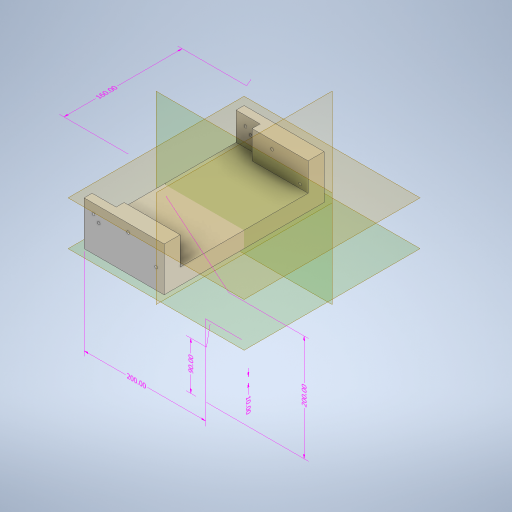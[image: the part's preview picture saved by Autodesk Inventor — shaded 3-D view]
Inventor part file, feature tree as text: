
AUTODESK INVENTOR PART (.ipt)
format: ipt  version: 2023 (Build 270158000, 158)  size: 448,000 bytes
history: native  units: mm
features: sketch x9, other x8, extrude x5, hole x4, plane x4, split x3
ambient origin geometry x8: Origin, YZ Plane, XZ Plane, XY Plane, X Axis, Y Axis, Z Axis, Center Point
bodies: Body1 (feature_tree)
feature tree (33):
  other  "Sólido1"
  other  "Anotaciones"
  extrude  "Extrusión1"  Depth=200.0mm
  hole  "Agujero1"  [1 undecoded]
  extrude  "Extrusión2"  Depth=15.0mm
  extrude  "Extrusión3"  Depth=20.0mm TaperAngle=0.0deg
  extrude  "Extrusión4"  Depth=200.0mm
  extrude  "Extrusión5"  Depth=20.0mm
  hole  "Agujero2"  [1 undecoded]
  plane  "Plano de trabajo1"
  split  "Dividir1"
  plane  "Plano de trabajo2"
  plane  "Plano de trabajo3"
  plane  "Plano de trabajo4"
  hole  "Agujero3"  [1 undecoded]
  hole  "Agujero4"  [1 undecoded]
  split  "Dividir2"
  split  "Dividir3"
  sketch  "Boceto2"  dims[d7=15.0mm d8=200.0mm]
  sketch  "Boceto3"  dims[d9=10.0mm d10=0.0mm]
  sketch  "Boceto4"  dims[d11=3.5mm d12=1.75mm d13=1.75mm d14=1.75mm d15=1.75mm d16=10.0mm d17=10.0mm d19=40.0mm]
  sketch  "Boceto5"  dims[d20=3.5mm d21=6.0mm d22=4.0mm d23=2.0mm d24=90.0deg d25=8.0mm d26=20.594885mm d27=15.0mm]
  sketch  "Boceto6"  dims[d28=20.0mm d29=80.0mm d30=0.0mm]
  sketch  "Boceto7"  dims[d31=57.0mm d32=200.0mm]
  sketch  "Boceto8"  dims[d33=110.0mm d34=0.0mm d36=20.0mm]
  sketch  "Boceto9"  dims[d37=20.0mm d38=20.0mm]
  sketch  "Boceto10"  dims[d39=90.0mm d40=0.0mm d43=30.0mm d44=0.0mm d45=3.5mm d46=1.75mm d47=1.75mm d48=1.75mm d49=1.75mm d50=10.0mm d51=10.0mm d52=15.0mm d53=10.0mm d54=10.0mm d55=15.0mm d56=3.5mm d57=6.0mm d58=4.0mm d59=2.0mm d60=90.0deg d61=8.0mm d62=20.594885mm d63=10.0mm d65=10.0mm d75=200.0mm d76=10.0mm d77=20.0mm d81=40.0mm d88=90.0deg d89=10.0mm d90=30.0mm d91=5.0mm d92=5.0mm d93=5.0mm d94=5.0mm d95=30.0mm d96=5.0mm d97=5.0mm d98=3.5mm d99=5.0mm d100=5.0mm d101=5.0mm d102=5.0mm d103=5.0mm d104=20.0mm d105=3.5mm d106=6.0mm d107=4.0mm d108=2.0mm d109=90.0deg d110=8.0mm d111=20.594885mm d112=10.0mm d113=30.0mm d114=5.0mm d115=5.0mm d116=5.0mm d117=5.0mm d118=5.0mm d119=5.0mm d120=3.5mm d121=5.0mm d122=5.0mm d123=5.0mm d124=5.0mm d125=5.0mm d126=30.0mm d127=30.0mm d128=3.5mm d129=6.0mm d130=4.0mm d131=2.0mm d132=90.0deg d133=8.0mm d134=20.594885mm d66=5.760865mm d67=7.72461mm d68=200.0mm d69=3.008686mm d70=2.422102mm d71=10.0mm d72=3.500509mm d73=2.402572mm d74=90.0mm d78=3.13122mm d79=6.269346mm d80=200.0mm d82=8.450127mm d83=0.968417mm d84=20.0mm d85=4.759975mm d86=4.646891mm d87=160.0mm]
  other  "Cota lineal 1"
  other  "Cota lineal 2"
  other  "Cota lineal 3"
  other  "Cota lineal 4"
  other  "Cota lineal 5"
  other  "Cota lineal 6"
note: 4 required parameter values undecoded (feature->parameter linkage not recoverable at this tier; creation-order binding heuristic only, values carry confidence <= 0.55)
